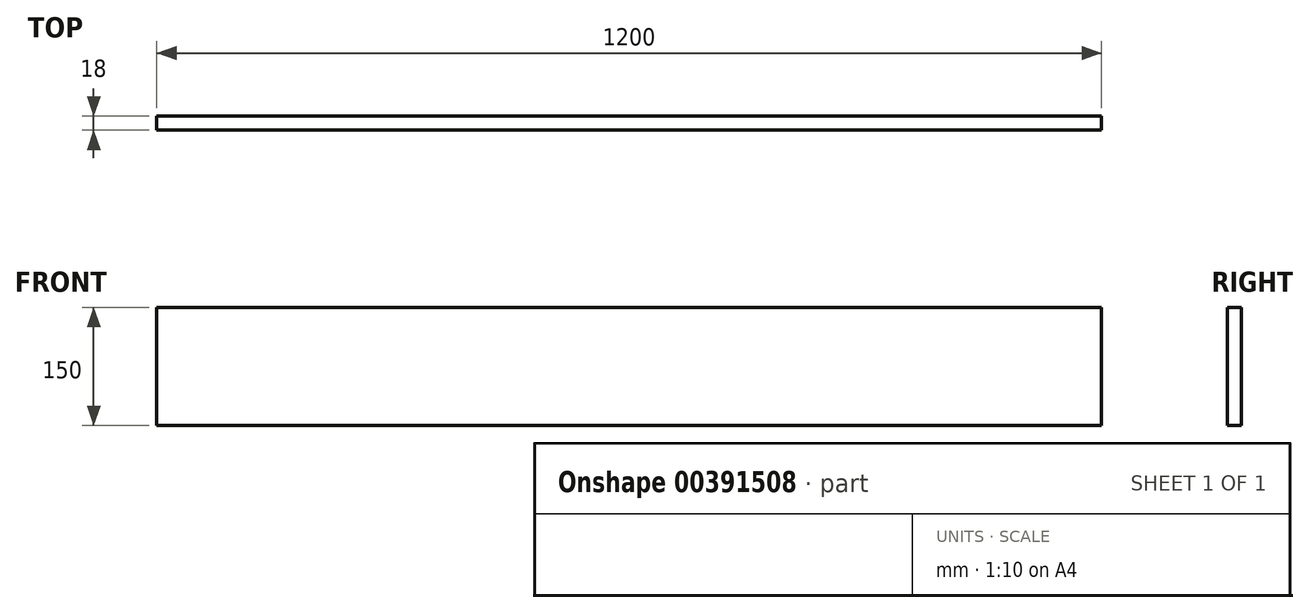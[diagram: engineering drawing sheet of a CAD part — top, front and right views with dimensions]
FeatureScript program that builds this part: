
annotation { "Feature Type Name" : "Feature", "Feature Type Description" : "" }
export const myFeature = defineFeature(function(context is Context, id is Id, definition is map)
    precondition{}
    {
        {
            var Q0;
            Q0=qCreatedBy(makeId("Front.planeOp"),FACE);
            var sketch = newSketch(context, id + "F0", { "sketchPlane" : qUnion([Q0])});
            skLineSegment(sketch, "E0.bottom", {"start": v(-600, 150) * mm, "end": v(600, 150) * mm});
            skLineSegment(sketch, "E0.top", {"start": v(-600, 0) * mm, "end": v(600, 0) * mm});
            skLineSegment(sketch, "E0.left", {"start": v(-600, 150) * mm, "end": v(-600, 0) * mm});
            skLineSegment(sketch, "E0.right", {"start": v(600, 150) * mm, "end": v(600, 0) * mm});
            skSolve(sketch);
        }
        {
            var Q0;
            Q0=makeQuery(id+"F0.imprint","IMPRINT",FACE,{"disambiguationData":[TD([[makeQuery(id+"F0.imprint","IMPRINT",EDGE,{"derivedFrom":sQuery(id+"F0.wireOp",EDGE,"E0.bottom")}),-1.0]])]});
            extrude(context, id + "F1", {"entities" : qUnion([Q0]), "depth" : 18 * mm});
        }
    });
